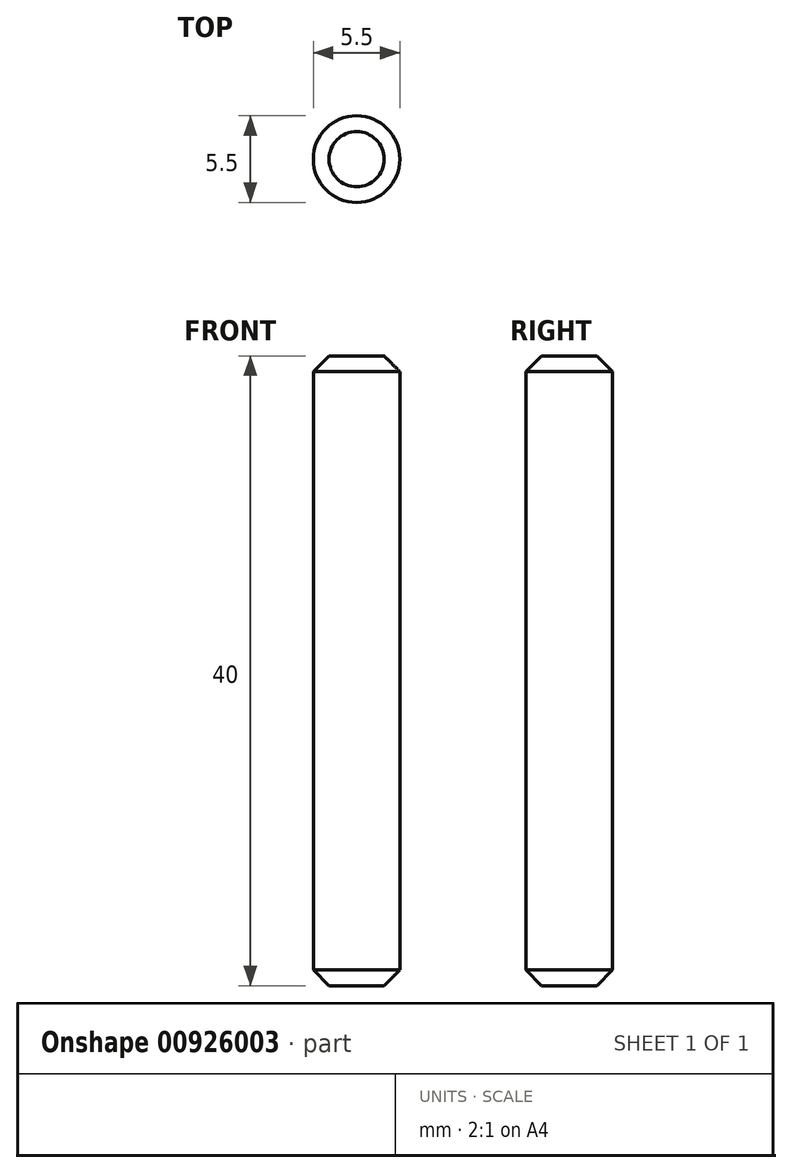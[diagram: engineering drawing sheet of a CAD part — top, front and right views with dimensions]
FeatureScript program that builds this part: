
annotation { "Feature Type Name" : "Feature", "Feature Type Description" : "" }
export const myFeature = defineFeature(function(context is Context, id is Id, definition is map)
    precondition{}
    {
        {
            var Q0;
            Q0=qCreatedBy(makeId("Top.planeOp"),FACE);
            var sketch = newSketch(context, id + "F0", { "sketchPlane" : qUnion([Q0])});
            skCircle(sketch, "E0", {"center": v(0, 0) * mm, "radius": 2.75 * mm});
            skSolve(sketch);
        }
        {
            var Q0;
            Q0 = qSketchRegion(id + "F0", true);
            extrude(context, id + "F1", {"entities" : qUnion([Q0]), "endBound" : BoundingType.SYMMETRIC, "depth" : 40 * mm, "offsetDistance" : 25 * mm});
        }
        {
            var Q0;
            Q0=makeQuery(id+"F1.opExtrude","CAP_EDGE",EDGE,{"disambiguationData":[OSD([sQuery(id+"F0.wireOp",EDGE,"E0")])],"isStart":false});
            var Q1;
            Q1=makeQuery(id+"F1.opExtrude","CAP_FACE",FACE,{"disambiguationData":[OSD([sQuery(id+"F0.wireOp",EDGE,"E0")])],"isStart":true});
            chamfer(context, id + "F2", {"entities" : qUnion([Q0, Q1]), "width" : 1 * mm, "tangentPropagation" : true});
        }
    });
